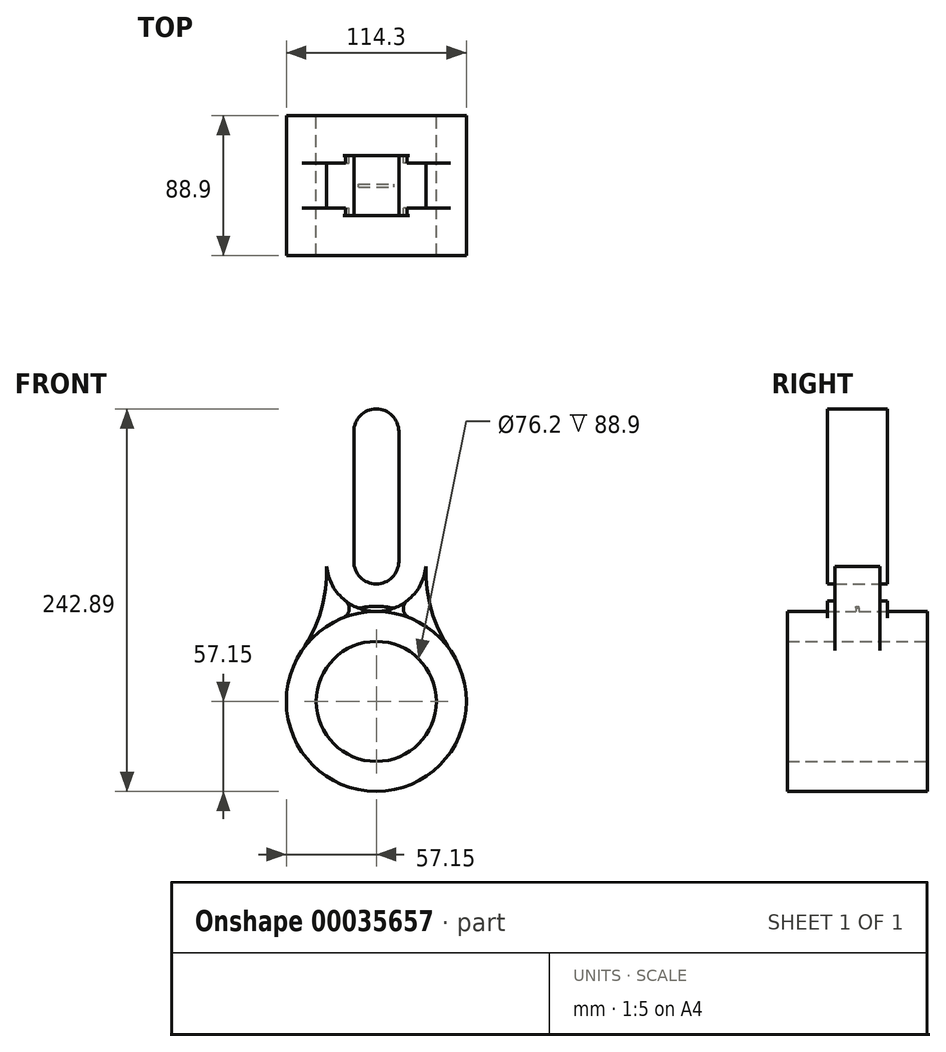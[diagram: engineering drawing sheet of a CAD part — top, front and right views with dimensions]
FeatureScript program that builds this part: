
annotation { "Feature Type Name" : "Feature", "Feature Type Description" : "" }
export const myFeature = defineFeature(function(context is Context, id is Id, definition is map)
    precondition{}
    {
        {
            var Q0;
            Q0=qCreatedBy(makeId("Front.planeOp"),FACE);
            var sketch = newSketch(context, id + "F0", { "sketchPlane" : qUnion([Q0])});
            skCircle(sketch, "E0", {"center": v(0, 0) * mm, "radius": 38.1 * mm});
            skCircle(sketch, "E1", {"center": v(0, 0) * mm, "radius": 57.15 * mm});
            skSolve(sketch);
        }
        {
            var Q0;
            Q0=makeQuery(id+"F0.imprint","IMPRINT",FACE,{"disambiguationData":[TD([[makeQuery(id+"F0.imprint","IMPRINT",EDGE,{"derivedFrom":sQuery(id+"F0.wireOp",EDGE,"E0")}),-1.0]])]});
            extrude(context, id + "F1", {"entities" : qUnion([Q0]), "endBound" : BoundingType.SYMMETRIC, "depth" : 88.9 * mm});
        }
        {
            var Q0;
            Q0=qCreatedBy(makeId("Front.planeOp"),FACE);
            var sketch = newSketch(context, id + "F2", { "sketchPlane" : qUnion([Q0])});
            skLineSegment(sketch, "E2", {"start": v(0, 88.9) * mm, "end": v(0, 171.45) * mm});
            skArc(sketch, "E3.0.startCap", {"start": v(14.29, 88.9) * mm, "mid": v(0, 74.61) * mm, "end": v(-14.29, 88.9) * mm});
            skArc(sketch, "E3.0.endCap", {"start": v(-14.29, 171.45) * mm, "mid": v(0, 185.74) * mm, "end": v(14.29, 171.45) * mm});
            skLineSegment(sketch, "E3.0.left", {"start": v(-14.29, 88.9) * mm, "end": v(-14.29, 171.45) * mm});
            skLineSegment(sketch, "E3.0.right", {"start": v(14.29, 88.9) * mm, "end": v(14.29, 171.45) * mm});
            skArc(sketch, "E4.0.startCap", {"start": v(31.75, 88.9) * mm, "mid": v(0, 57.15) * mm, "end": v(-31.75, 88.9) * mm});
            skArc(sketch, "E4.0.endCap", {"start": v(-31.75, 171.45) * mm, "mid": v(0, 203.2) * mm, "end": v(31.75, 171.45) * mm});
            skLineSegment(sketch, "E4.0.left", {"start": v(-31.75, 88.9) * mm, "end": v(-31.75, 171.45) * mm});
            skLineSegment(sketch, "E4.0.right", {"start": v(31.75, 88.9) * mm, "end": v(31.75, 171.45) * mm});
            skCircle(sketch, "E5.0", {"center": v(0, 0) * mm, "radius": 57.15 * mm});
            skArc(sketch, "E6", {"start": v(19.64, 63.95) * mm, "mid": v(17.28, 58.06) * mm, "end": v(21.21, 53.07) * mm});
            skArc(sketch, "E7", {"start": v(-21.21, 53.07) * mm, "mid": v(-17.28, 58.06) * mm, "end": v(-19.64, 63.95) * mm});
            skSolve(sketch);
        }
        {
            var Q0;
            Q0=makeQuery(id+"F2.imprint","IMPRINT",FACE,{"disambiguationData":[TD([[makeQuery(id+"F2.imprint","IMPRINT",EDGE,{"derivedFrom":sQuery(id+"F2.wireOp",EDGE,"E3.0.startCap")}),1.0]])]});
            var Q1;
            {var subQ0=sQuery(id+"F2.wireOp",EDGE,"E7");Q1=makeQuery(id+"F2.imprint","IMPRINT",FACE,{"disambiguationData":[TD([[makeQuery(id+"F2.imprint","IMPRINT",EDGE,{"derivedFrom":subQ0}),-1.0]])]});}
            var Q2;
            {var subQ0=sQuery(id+"F2.wireOp",EDGE,"E6");Q2=makeQuery(id+"F2.imprint","IMPRINT",FACE,{"disambiguationData":[TD([[makeQuery(id+"F2.imprint","IMPRINT",EDGE,{"derivedFrom":subQ0}),-1.0]])]});}
            extrude(context, id + "F3", {"entities" : qUnion([Q0, Q1, Q2]), "operationType" : NewBodyOperationType.ADD, "endBound" : BoundingType.SYMMETRIC, "depth" : 38.1 * mm});
        }
        {
            var Q0;
            Q0=qCreatedBy(makeId("Front.planeOp"),FACE);
            var sketch = newSketch(context, id + "F4", { "sketchPlane" : qUnion([Q0])});
            skLineSegment(sketch, "E8.0", {"start": v(31.75, 88.9) * mm, "end": v(31.75, 171.45) * mm});
            skCircle(sketch, "E9.0", {"center": v(0, 0) * mm, "radius": 57.15 * mm});
            skLineSegment(sketch, "E10.0", {"start": v(-31.75, 88.9) * mm, "end": v(-31.75, 171.45) * mm});
            skArc(sketch, "E11", {"start": v(31.75, 88.9) * mm, "mid": v(34.64, 59.31) * mm, "end": v(47.12, 32.33) * mm});
            skArc(sketch, "E12", {"start": v(-47.12, 32.33) * mm, "mid": v(-34.64, 59.31) * mm, "end": v(-31.75, 88.9) * mm});
            skArc(sketch, "E13.0", {"start": v(-21.21, 53.07) * mm, "mid": v(-17.28, 58.06) * mm, "end": v(-19.64, 63.95) * mm});
            skArc(sketch, "E14.0", {"start": v(-19.64, 63.95) * mm, "mid": v(-28.56, 75.03) * mm, "end": v(-31.75, 88.9) * mm});
            skArc(sketch, "E15.0", {"start": v(31.75, 88.9) * mm, "mid": v(28.56, 75.03) * mm, "end": v(19.64, 63.95) * mm});
            skArc(sketch, "E16.0", {"start": v(19.64, 63.95) * mm, "mid": v(17.28, 58.06) * mm, "end": v(21.21, 53.07) * mm});
            skSolve(sketch);
        }
        {
            var Q0;
            {var subQ3=sQuery(id+"F4.wireOp",EDGE,"E13.0");Q0=makeQuery(id+"F4.imprint","IMPRINT",FACE,{"disambiguationData":[TD([[makeQuery(id+"F4.imprint","IMPRINT",EDGE,{"derivedFrom":subQ3}),1.0]])]});}
            var Q1;
            {var subQ0=sQuery(id+"F4.wireOp",EDGE,"E16.0");Q1=makeQuery(id+"F4.imprint","IMPRINT",FACE,{"disambiguationData":[TD([[makeQuery(id+"F4.imprint","IMPRINT",EDGE,{"derivedFrom":subQ0}),1.0]])]});}
            extrude(context, id + "F5", {"entities" : qUnion([Q0, Q1]), "operationType" : NewBodyOperationType.ADD, "endBound" : BoundingType.SYMMETRIC, "depth" : 28.57 * mm});
        }
        {
            var Q0;
            Q0=qCreatedBy(makeId("Front.planeOp"),FACE);
            var sketch = newSketch(context, id + "F6", { "sketchPlane" : qUnion([Q0])});
            skArc(sketch, "E17.0", {"start": v(-21.21, 53.07) * mm, "mid": v(-17.28, 58.06) * mm, "end": v(-19.64, 63.95) * mm});
            skArc(sketch, "E18.0", {"start": v(19.64, 63.95) * mm, "mid": v(17.28, 58.06) * mm, "end": v(21.21, 53.07) * mm});
            skArc(sketch, "E19", {"start": v(17.33, 57.78) * mm, "mid": v(0, 60.33) * mm, "end": v(-17.33, 57.78) * mm});
            skCircle(sketch, "E20.0", {"center": v(0, 0) * mm, "radius": 57.15 * mm});
            skSolve(sketch);
        }
        {
            var Q0;
            {var subQ5=sQuery(id+"F6.wireOp",EDGE,"E19");Q0=makeQuery(id+"F6.imprint","IMPRINT",FACE,{"disambiguationData":[TD([[makeQuery(id+"F6.imprint","IMPRINT",EDGE,{"derivedFrom":subQ5}),1.0]])]});}
            extrude(context, id + "F7", {"entities" : qUnion([Q0]), "operationType" : NewBodyOperationType.ADD, "endBound" : BoundingType.SYMMETRIC, "depth" : (1 + 1 / 8 + 2 * (5 / 16)) * mm});
        }
    });
